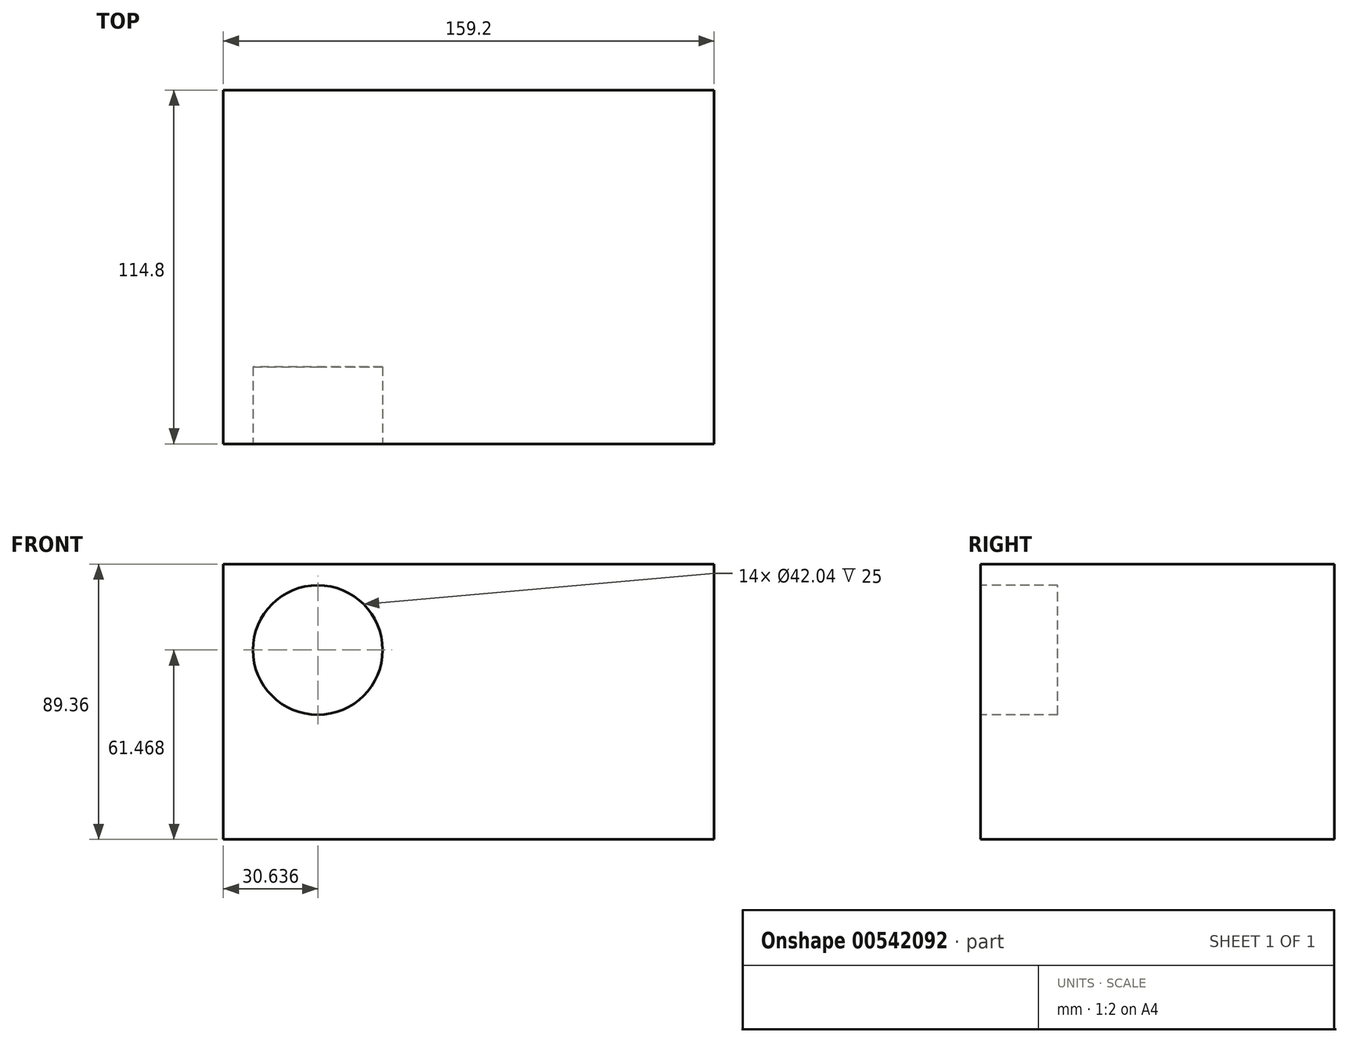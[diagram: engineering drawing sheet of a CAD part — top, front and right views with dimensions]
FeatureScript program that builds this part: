
annotation { "Feature Type Name" : "Feature", "Feature Type Description" : "" }
export const myFeature = defineFeature(function(context is Context, id is Id, definition is map)
    precondition{}
    {
        {
            var Q0;
            Q0=qCreatedBy(makeId("Front.planeOp"),FACE);
            var sketch = newSketch(context, id + "F0", { "sketchPlane" : qUnion([Q0])});
            skLineSegment(sketch, "E0.bottom", {"start": v(-68, 60.66) * mm, "end": v(91.2, 60.66) * mm});
            skLineSegment(sketch, "E0.top", {"start": v(-68, -28.7) * mm, "end": v(91.2, -28.7) * mm});
            skLineSegment(sketch, "E0.left", {"start": v(-68, 60.66) * mm, "end": v(-68, -28.7) * mm});
            skLineSegment(sketch, "E0.right", {"start": v(91.2, 60.66) * mm, "end": v(91.2, -28.7) * mm});
            skSolve(sketch);
        }
        {
            var Q0;
            Q0 = qSketchRegion(id + "F0", true);
            extrude(context, id + "F1", {"entities" : qUnion([Q0]), "depth" : 114.8 * mm, "offsetDistance" : 25 * mm});
        }
        {
            var Q0;
            Q0=makeQuery(id+"F1.opExtrude","CAP_FACE",FACE,{"disambiguationData":[OSD([sQuery(id+"F0.wireOp",EDGE,"E0.bottom"),sQuery(id+"F0.wireOp",EDGE,"E0.top"),sQuery(id+"F0.wireOp",EDGE,"E0.left"),sQuery(id+"F0.wireOp",EDGE,"E0.right")])],"isStart":false});
            var sketch = newSketch(context, id + "F2", { "sketchPlane" : qUnion([Q0])});
            skCircle(sketch, "E1", {"center": v(-37.37, 32.77) * mm, "radius": 21.02 * mm});
            skSolve(sketch);
        }
        {
            var Q0;
            Q0 = qSketchRegion(id + "F2", true);
            extrude(context, id + "F3", {"entities" : qUnion([Q0]), "operationType" : NewBodyOperationType.REMOVE, "oppositeDirection" : true, "depth" : 25 * mm, "offsetDistance" : 25 * mm});
        }
    });
